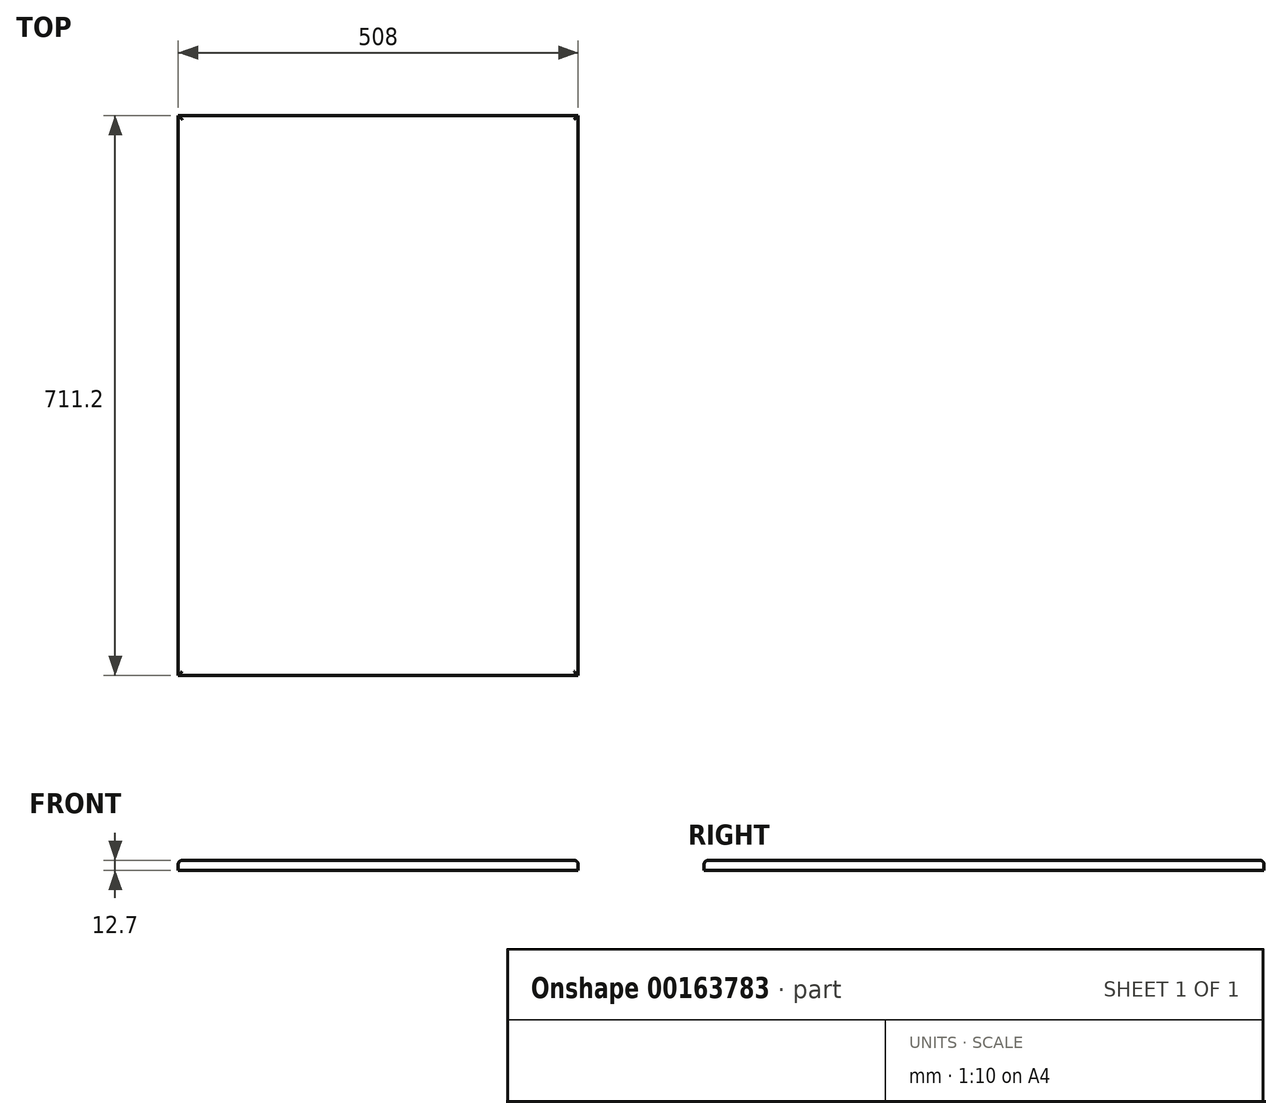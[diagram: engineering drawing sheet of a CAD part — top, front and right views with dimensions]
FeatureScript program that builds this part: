
annotation { "Feature Type Name" : "Feature", "Feature Type Description" : "" }
export const myFeature = defineFeature(function(context is Context, id is Id, definition is map)
    precondition{}
    {
        {
            var Q0;
            Q0=qCreatedBy(makeId("Top.planeOp"),FACE);
            var sketch = newSketch(context, id + "F0", { "sketchPlane" : qUnion([Q0])});
            skLineSegment(sketch, "E0.bottom", {"start": v(254, -355.6) * mm, "end": v(-254, -355.6) * mm});
            skLineSegment(sketch, "E0.top", {"start": v(254, 355.6) * mm, "end": v(-254, 355.6) * mm});
            skLineSegment(sketch, "E0.left", {"start": v(254, -355.6) * mm, "end": v(254, 355.6) * mm});
            skLineSegment(sketch, "E0.right", {"start": v(-254, -355.6) * mm, "end": v(-254, 355.6) * mm});
            skPoint(sketch, "E0.middle", {"position": v(0, 0) * mm});
            skSolve(sketch);
        }
        {
            var Q0;
            Q0=qSketchRegion(id+"F0",true);
            extrude(context, id + "F1", {"entities" : qUnion([Q0]), "depth" : 12.7 * mm});
        }
        {
            var Q0;
            Q0=makeQuery(id+"F1.opExtrude","CAP_FACE",FACE,{"disambiguationData":[OSD([sQuery(id+"F0.wireOp",EDGE,"E0.bottom"),sQuery(id+"F0.wireOp",EDGE,"E0.top"),sQuery(id+"F0.wireOp",EDGE,"E0.left"),sQuery(id+"F0.wireOp",EDGE,"E0.right")])],"isStart":false});
            fillet(context, id + "F2", {"entities" : qUnion([Q0]), "radius" : 5.08 * mm, "tangentPropagation" : true, "allowEdgeOverflow" : false});
        }
    });
